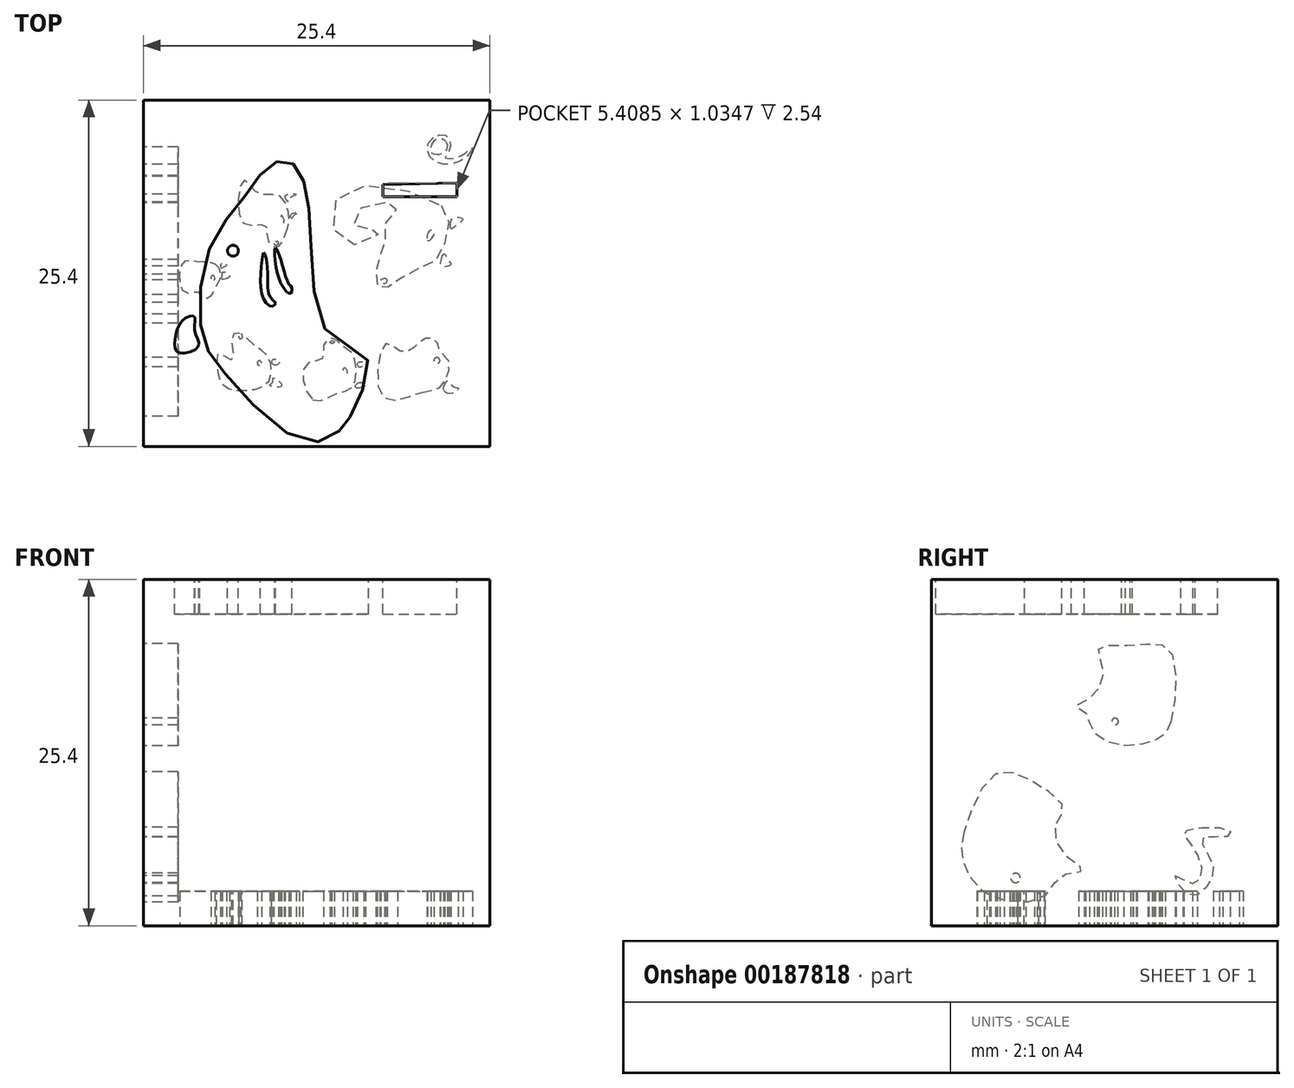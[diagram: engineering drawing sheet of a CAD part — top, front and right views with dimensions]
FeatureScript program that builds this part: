
annotation { "Feature Type Name" : "Feature", "Feature Type Description" : "" }
export const myFeature = defineFeature(function(context is Context, id is Id, definition is map)
    precondition{}
    {
        {
            var Q0;
            Q0=qCreatedBy(makeId("Front.planeOp"),FACE);
            var sketch = newSketch(context, id + "F0", { "sketchPlane" : qUnion([Q0])});
            skLineSegment(sketch, "E0.bottom", {"start": v(12.7, 12.7) * mm, "end": v(-12.7, 12.7) * mm});
            skLineSegment(sketch, "E0.top", {"start": v(12.7, -12.7) * mm, "end": v(-12.7, -12.7) * mm});
            skLineSegment(sketch, "E0.left", {"start": v(12.7, 12.7) * mm, "end": v(12.7, -12.7) * mm});
            skLineSegment(sketch, "E0.right", {"start": v(-12.7, 12.7) * mm, "end": v(-12.7, -12.7) * mm});
            skPoint(sketch, "E0.middle", {"position": v(0, 0) * mm});
            skSolve(sketch);
        }
        {
            var Q0;
            Q0 = qSketchRegion(id + "F0", true);
            extrude(context, id + "F1", {"entities" : qUnion([Q0]), "depth" : 25.4 * mm});
        }
        {
            var Q0;
            Q0=makeQuery(id+"F1.opExtrude","SWEPT_FACE",FACE,{"disambiguationData":[OSD([sQuery(id+"F0.wireOp",EDGE,"E0.bottom")])]});
            var sketch = newSketch(context, id + "F2", { "sketchPlane" : qUnion([Q0])});
            skFitSpline(sketch, "E1", {"points": [v(-6.7, -20.08) * mm, v(-8.4, -17.21) * mm, v(-7.88, -10.96) * mm, v(-5.3, -7.1) * mm, v(-3.55, -4.9) * mm, v(-2.1, -4.47) * mm, v(-1.06, -5.7) * mm, v(-0.45, -9.83) * mm, v(0.96, -17.26) * mm, v(3.7, -18.96) * mm, v(2.61, -22.9) * mm, v(1.72, -24.22) * mm, v(-0.87, -25.02) * mm, v(-6.7, -20.08) * mm]});
            skLineSegment(sketch, "E2", {"start": v(4.87, -7.1) * mm, "end": v(10.28, -7.1) * mm});
            skLineSegment(sketch, "E3", {"start": v(10.28, -7.1) * mm, "end": v(10.28, -6.07) * mm});
            skLineSegment(sketch, "E4", {"start": v(4.87, -7.1) * mm, "end": v(4.87, -6.2) * mm});
            skLineSegment(sketch, "E5", {"start": v(4.87, -6.2) * mm, "end": v(10.28, -6.07) * mm});
            skCircle(sketch, "E6", {"center": v(-6.14, -11.05) * mm, "radius": 0.4 * mm});
            skFitSpline(sketch, "E7", {"points": [v(-3.87, -11.18) * mm, v(-4.1, -12.55) * mm, v(-3.9, -14.57) * mm, v(-3.26, -15.14) * mm, v(-3.03, -14.87) * mm, v(-3.4, -14.45) * mm, v(-3.6, -12.62) * mm, v(-3.87, -11.18) * mm]});
            skFitSpline(sketch, "E8", {"points": [v(-3.03, -10.83) * mm, v(-3, -12.13) * mm, v(-2.42, -13.8) * mm, v(-1.92, -14.19) * mm, v(-1.8, -13.8) * mm, v(-2.08, -13.42) * mm, v(-2.53, -12.05) * mm, v(-3.03, -10.83) * mm]});
            skFitSpline(sketch, "E9", {"points": [v(-8.67, -18.06) * mm, v(-8.94, -16.94) * mm, v(-8.98, -15.9) * mm, v(-9.8, -16.13) * mm, v(-10.4, -17.55) * mm, v(-10.13, -18.54) * mm, v(-8.67, -18.06) * mm]});
            skSolve(sketch);
        }
        {
            var Q0;
            Q0=makeQuery(id+"F2.imprint","IMPRINT",FACE,{"disambiguationData":[TD([[makeQuery(id+"F2.imprint","IMPRINT",EDGE,{"derivedFrom":sQuery(id+"F2.wireOp",EDGE,"25fdf307-3059-4b63-b4c4-ef75757527ce")}),-1.0]])]});
            var Q1;
            Q1=makeQuery(id+"F2.imprint","IMPRINT",FACE,{"disambiguationData":[TD([[makeQuery(id+"F2.imprint","IMPRINT",EDGE,{"derivedFrom":sQuery(id+"F2.wireOp",EDGE,"E2")}),1.0]])]});
            var Q2;
            Q2=makeQuery(id+"F2.imprint","IMPRINT",FACE,{"disambiguationData":[TD([[makeQuery(id+"F2.imprint","IMPRINT",EDGE,{"derivedFrom":sQuery(id+"F2.wireOp",EDGE,"E1")}),-1.0]])]});
            var Q3;
            Q3=makeQuery(id+"F2.imprint","IMPRINT",FACE,{"disambiguationData":[TD([[makeQuery(id+"F2.imprint","IMPRINT",EDGE,{"derivedFrom":sQuery(id+"F2.wireOp",EDGE,"E9")}),1.0]])]});
            extrude(context, id + "F3", {"entities" : qUnion([Q0, Q1, Q2, Q3]), "operationType" : NewBodyOperationType.REMOVE, "oppositeDirection" : true, "depth" : 2.54 * mm});
        }
        {
            var Q0;
            Q0=makeQuery(id+"F1.opExtrude","SWEPT_FACE",FACE,{"disambiguationData":[OSD([sQuery(id+"F0.wireOp",EDGE,"E0.right")])]});
            var sketch = newSketch(context, id + "F4", { "sketchPlane" : qUnion([Q0])});
            skFitSpline(sketch, "E10", {"points": [v(23, -5.85) * mm, v(23.11, -7.79) * mm, v(21.38, -10.34) * mm, v(17.14, -10.56) * mm, v(15.85, -9.01) * mm, v(14.26, -8.65) * mm, v(15.7, -7.43) * mm, v(16.24, -5.13) * mm, v(15.7, -4.08) * mm, v(18.22, -2) * mm, v(20.84, -1.68) * mm, v(23, -5.85) * mm]});
            skFitSpline(sketch, "E11", {"points": [v(7.83, 2.28) * mm, v(8.62, 1.1) * mm, v(11.35, 0.52) * mm, v(13.62, 1.67) * mm, v(14.05, 2.9) * mm, v(14.84, 3.36) * mm, v(13.76, 4) * mm, v(12.79, 6.13) * mm, v(13.15, 7.6) * mm, v(10.52, 7.89) * mm, v(7.9, 7.5) * mm, v(7.83, 2.28) * mm]});
            skCircle(sketch, "E12", {"center": v(19.23, -9.2) * mm, "radius": 0.35 * mm});
            skCircle(sketch, "E13", {"center": v(11.93, 2.27) * mm, "radius": 0.24 * mm});
            skFitSpline(sketch, "E14", {"points": [v(7.52, -9.03) * mm, v(6.26, -9.6) * mm, v(5.55, -8.62) * mm, v(6.6, -6.38) * mm, v(6.8, -5.77) * mm, v(3.55, -5.7) * mm, v(3.65, -6.15) * mm, v(5.55, -6.28) * mm, v(4.87, -7.94) * mm, v(5, -9.54) * mm, v(6.47, -10.49) * mm, v(7.52, -9.03) * mm]});
            skSolve(sketch);
        }
        {
            var Q0;
            Q0 = qSketchRegion(id + "F4", true);
            extrude(context, id + "F5", {"entities" : qUnion([Q0]), "operationType" : NewBodyOperationType.REMOVE, "oppositeDirection" : true, "depth" : 2.54 * mm});
        }
        {
            var Q0;
            Q0=makeQuery(id+"F1.opExtrude","SWEPT_FACE",FACE,{"disambiguationData":[OSD([sQuery(id+"F0.wireOp",EDGE,"E0.top")])]});
            var sketch = newSketch(context, id + "F6", { "sketchPlane" : qUnion([Q0])});
            skFitSpline(sketch, "E15", {"points": [v(7.72, 21.44) * mm, v(9.16, 20.98) * mm, v(9.7, 19.2) * mm, v(9.06, 18.45) * mm, v(8.74, 17.62) * mm, v(7.88, 17.52) * mm, v(7.06, 18.22) * mm, v(6.08, 18.4) * mm, v(5.04, 17.87) * mm, v(4.82, 21.73) * mm, v(7.72, 21.44) * mm]});
            skFitSpline(sketch, "E16", {"points": [v(9.3, 21.23) * mm, v(9.65, 20.58) * mm, v(10, 21) * mm, v(10.39, 21.14) * mm, v(9.9, 21.52) * mm, v(9.3, 21.23) * mm]});
            skFitSpline(sketch, "E17", {"points": [v(9.13, 7.74) * mm, v(9.62, 9.43) * mm, v(8.76, 11.74) * mm, v(6.99, 12.55) * mm, v(5.47, 13.6) * mm, v(4.68, 13.8) * mm, v(4.38, 13.32) * mm, v(4.64, 11.4) * mm, v(5.06, 10.4) * mm, v(5.06, 9) * mm, v(5.92, 7.79) * mm, v(3.25, 7.94) * mm, v(2.9, 9.37) * mm, v(4.7, 9.56) * mm, v(2.22, 10.57) * mm, v(1.73, 6.91) * mm, v(9.13, 7.74) * mm]});
            skFitSpline(sketch, "E18", {"points": [v(9.85, 9.43) * mm, v(10, 8.66) * mm, v(10.7, 8.75) * mm, v(10.28, 9.13) * mm, v(9.85, 9.43) * mm]});
            skFitSpline(sketch, "E19", {"points": [v(9.13, 11.72) * mm, v(9.36, 11.3) * mm, v(9.62, 11.72) * mm, v(9.83, 12.08) * mm, v(9.21, 12.2) * mm, v(9.13, 11.72) * mm]});
            skCircle(sketch, "E20", {"center": v(8.81, 19.11) * mm, "radius": 0.22 * mm});
            skFitSpline(sketch, "E21", {"points": [v(8.12, 10.29) * mm, v(8.46, 10.12) * mm, v(8.57, 9.58) * mm, v(8.25, 9.63) * mm, v(8.12, 10.29) * mm]});
            skFitSpline(sketch, "E22", {"points": [v(-0.29, 21.97) * mm, v(1.4, 21.55) * mm, v(2.71, 20.91) * mm, v(2.63, 18.62) * mm, v(1.95, 18.11) * mm, v(1.26, 17.48) * mm, v(0.55, 17.9) * mm, v(0.4, 18.97) * mm, v(-0.84, 19.46) * mm, v(-0.29, 21.97) * mm]});
            skFitSpline(sketch, "E23", {"points": [v(2.89, 21.1) * mm, v(3.08, 20.73) * mm, v(3.57, 20.9) * mm, v(2.89, 21.1) * mm]});
            skFitSpline(sketch, "E24", {"points": [v(2.22, 20.06) * mm, v(2.1, 19.67) * mm, v(1.92, 19.8) * mm, v(2.22, 20.06) * mm]});
            skFitSpline(sketch, "E25", {"points": [v(-2.27, 9.82) * mm, v(-2.03, 8.85) * mm, v(-2.68, 7.05) * mm, v(-4.35, 6.81) * mm, v(-5.35, 5.91) * mm, v(-5.41, 9) * mm, v(-3.81, 9.17) * mm, v(-3.58, 10.3) * mm, v(-2.85, 10.76) * mm, v(-2.27, 9.82) * mm]});
            skFitSpline(sketch, "E26", {"points": [v(-2.07, 7.46) * mm, v(-2.3, 7.01) * mm, v(-1.49, 6.93) * mm, v(-2.01, 7.24) * mm, v(-2.07, 7.46) * mm]});
            skFitSpline(sketch, "E27", {"points": [v(-2.44, 8.97) * mm, v(-2.38, 8.8) * mm, v(-2.6, 8.47) * mm, v(-2.44, 8.97) * mm]});
            skFitSpline(sketch, "E28", {"points": [v(5.1, 13.41) * mm, v(5.07, 13.1) * mm, v(4.65, 13.31) * mm, v(5.1, 13.41) * mm]});
            skFitSpline(sketch, "E29", {"points": [v(11.42, 3.5) * mm, v(10.7, 4.4) * mm, v(8.55, 4.42) * mm, v(8.26, 3.03) * mm, v(9.52, 2.63) * mm, v(9.73, 3.73) * mm, v(9.39, 4.2) * mm, v(9.88, 4.29) * mm, v(10.95, 3.85) * mm, v(11.42, 3.5) * mm]});
            skFitSpline(sketch, "E30", {"points": [v(9.46, 3.03) * mm, v(9.39, 3.82) * mm, v(8.43, 3.87) * mm, v(8.74, 2.9) * mm, v(9.46, 3.03) * mm]});
            skFitSpline(sketch, "E31", {"points": [v(-7.28, 19.83) * mm, v(-7.06, 20.59) * mm, v(-6.52, 21.14) * mm, v(-5.37, 21.29) * mm, v(-3.93, 21.02) * mm, v(-3.32, 20.05) * mm, v(-3.66, 18.7) * mm, v(-4.54, 18.01) * mm, v(-5.64, 17.1) * mm, v(-6.22, 17.37) * mm, v(-6.2, 19.06) * mm, v(-7.17, 18.6) * mm, v(-7.28, 19.83) * mm]});
            skFitSpline(sketch, "E32", {"points": [v(-3.43, 20.93) * mm, v(-3.21, 20.68) * mm, v(-3.18, 20.37) * mm, v(-2.57, 20.96) * mm, v(-3.43, 20.93) * mm]});
            skFitSpline(sketch, "E33", {"points": [v(-5.64, 17.51) * mm, v(-5.64, 17.1) * mm, v(-5.46, 17.4) * mm, v(-5.64, 17.51) * mm]});
            skCircle(sketch, "E34", {"center": v(-4.2, 19.3) * mm, "radius": 0.16 * mm});
            skFitSpline(sketch, "E35", {"points": [v(-3.1, 19.45) * mm, v(-3.25, 19.06) * mm, v(-2.7, 19.17) * mm, v(-3.1, 19.45) * mm]});
            skFitSpline(sketch, "E36", {"points": [v(1.26, 17.65) * mm, v(1.2, 17.84) * mm, v(0.99, 17.75) * mm, v(1.26, 17.65) * mm]});
            skFitSpline(sketch, "E37", {"points": [v(-3.14, 10.52) * mm, v(-2.85, 10.6) * mm, v(-2.85, 10.39) * mm, v(-3.14, 10.52) * mm]});
            skFitSpline(sketch, "E38", {"points": [v(3.1, 19.6) * mm, v(3.06, 19.23) * mm, v(3.45, 19.32) * mm, v(3.1, 19.6) * mm]});
            skFitSpline(sketch, "E39", {"points": [v(-1.86, 8.7) * mm, v(-1.88, 8.39) * mm, v(-1.28, 8.25) * mm, v(-1.64, 8.44) * mm, v(-1.86, 8.7) * mm]});
            skFitSpline(sketch, "E40", {"points": [v(-7.46, 12.02) * mm, v(-7.05, 12.92) * mm, v(-7.53, 13.9) * mm, v(-7.83, 14.46) * mm, v(-8.4, 14.53) * mm, v(-8.66, 14.1) * mm, v(-9.7, 14.1) * mm, v(-9.8, 11.95) * mm, v(-8.83, 11.82) * mm, v(-7.46, 12.02) * mm]});
            skFitSpline(sketch, "E41", {"points": [v(-7.5, 13.2) * mm, v(-7.54, 12.89) * mm, v(-7.73, 12.94) * mm, v(-7.73, 13.14) * mm, v(-7.5, 13.2) * mm]});
            skFitSpline(sketch, "E42", {"points": [v(-6.97, 13.14) * mm, v(-6.92, 12.92) * mm, v(-6.88, 12.62) * mm, v(-6.37, 12.92) * mm, v(-6.97, 13.14) * mm]});
            skFitSpline(sketch, "E43", {"points": [v(-7.05, 12.07) * mm, v(-6.98, 12.3) * mm, v(-6.6, 12.05) * mm, v(-6.83, 11.97) * mm, v(-7.05, 12.07) * mm]});
            skSolve(sketch);
        }
        {
            var Q0;
            Q0=makeQuery(id+"F6.imprint","IMPRINT",FACE,{"disambiguationData":[TD([[makeQuery(id+"F6.imprint","IMPRINT",EDGE,{"derivedFrom":sQuery(id+"F6.wireOp",EDGE,"E15")}),-1.0]])]});
            var Q1;
            Q1=makeQuery(id+"F6.imprint","IMPRINT",FACE,{"disambiguationData":[TD([[makeQuery(id+"F6.imprint","IMPRINT",EDGE,{"derivedFrom":sQuery(id+"F6.wireOp",EDGE,"E16")}),1.0]])]});
            var Q2;
            Q2=makeQuery(id+"F6.imprint","IMPRINT",FACE,{"disambiguationData":[TD([[makeQuery(id+"F6.imprint","IMPRINT",EDGE,{"derivedFrom":sQuery(id+"F6.wireOp",EDGE,"E17")}),1.0]])]});
            var Q3;
            Q3=makeQuery(id+"F6.imprint","IMPRINT",FACE,{"disambiguationData":[TD([[makeQuery(id+"F6.imprint","IMPRINT",EDGE,{"derivedFrom":sQuery(id+"F6.wireOp",EDGE,"E19")}),1.0]])]});
            var Q4;
            Q4=makeQuery(id+"F6.imprint","IMPRINT",FACE,{"disambiguationData":[TD([[makeQuery(id+"F6.imprint","IMPRINT",EDGE,{"derivedFrom":sQuery(id+"F6.wireOp",EDGE,"E18")}),1.0]])]});
            var Q5;
            Q5=makeQuery(id+"F6.imprint","IMPRINT",FACE,{"disambiguationData":[TD([[makeQuery(id+"F6.imprint","IMPRINT",EDGE,{"derivedFrom":sQuery(id+"F6.wireOp",EDGE,"E29")}),1.0]])]});
            var Q6;
            Q6=makeQuery(id+"F6.imprint","IMPRINT",FACE,{"disambiguationData":[TD([[makeQuery(id+"F6.imprint","IMPRINT",EDGE,{"derivedFrom":sQuery(id+"F6.wireOp",EDGE,"E22")}),-1.0]])]});
            var Q7;
            Q7=makeQuery(id+"F6.imprint","IMPRINT",FACE,{"disambiguationData":[TD([[makeQuery(id+"F6.imprint","IMPRINT",EDGE,{"derivedFrom":sQuery(id+"F6.wireOp",EDGE,"E23")}),1.0]])]});
            var Q8;
            Q8=makeQuery(id+"F6.imprint","IMPRINT",FACE,{"disambiguationData":[TD([[makeQuery(id+"F6.imprint","IMPRINT",EDGE,{"derivedFrom":sQuery(id+"F6.wireOp",EDGE,"E38")}),1.0]])]});
            var Q9;
            Q9=makeQuery(id+"F6.imprint","IMPRINT",FACE,{"disambiguationData":[TD([[makeQuery(id+"F6.imprint","IMPRINT",EDGE,{"derivedFrom":sQuery(id+"F6.wireOp",EDGE,"E34")}),-1.0]])]});
            var Q10;
            Q10=makeQuery(id+"F6.imprint","IMPRINT",FACE,{"disambiguationData":[TD([[makeQuery(id+"F6.imprint","IMPRINT",EDGE,{"derivedFrom":sQuery(id+"F6.wireOp",EDGE,"E32")}),1.0]])]});
            var Q11;
            Q11=makeQuery(id+"F6.imprint","IMPRINT",FACE,{"disambiguationData":[TD([[makeQuery(id+"F6.imprint","IMPRINT",EDGE,{"derivedFrom":sQuery(id+"F6.wireOp",EDGE,"E35")}),1.0]])]});
            var Q12;
            Q12=makeQuery(id+"F6.imprint","IMPRINT",FACE,{"disambiguationData":[TD([[makeQuery(id+"F6.imprint","IMPRINT",EDGE,{"derivedFrom":sQuery(id+"F6.wireOp",EDGE,"E40")}),1.0]])]});
            var Q13;
            Q13=makeQuery(id+"F6.imprint","IMPRINT",FACE,{"disambiguationData":[TD([[makeQuery(id+"F6.imprint","IMPRINT",EDGE,{"derivedFrom":sQuery(id+"F6.wireOp",EDGE,"E42")}),1.0]])]});
            var Q14;
            Q14=makeQuery(id+"F6.imprint","IMPRINT",FACE,{"disambiguationData":[TD([[makeQuery(id+"F6.imprint","IMPRINT",EDGE,{"derivedFrom":sQuery(id+"F6.wireOp",EDGE,"E43")}),-1.0]])]});
            var Q15;
            Q15=makeQuery(id+"F6.imprint","IMPRINT",FACE,{"disambiguationData":[TD([[makeQuery(id+"F6.imprint","IMPRINT",EDGE,{"derivedFrom":sQuery(id+"F6.wireOp",EDGE,"E25")}),-1.0]])]});
            var Q16;
            Q16=makeQuery(id+"F6.imprint","IMPRINT",FACE,{"disambiguationData":[TD([[makeQuery(id+"F6.imprint","IMPRINT",EDGE,{"derivedFrom":sQuery(id+"F6.wireOp",EDGE,"E39")}),1.0]])]});
            var Q17;
            Q17=makeQuery(id+"F6.imprint","IMPRINT",FACE,{"disambiguationData":[TD([[makeQuery(id+"F6.imprint","IMPRINT",EDGE,{"derivedFrom":sQuery(id+"F6.wireOp",EDGE,"E26")}),1.0]])]});
            extrude(context, id + "F7", {"entities" : qUnion([Q0, Q1, Q2, Q3, Q4, Q5, Q6, Q7, Q8, Q9, Q10, Q11, Q12, Q13, Q14, Q15, Q16, Q17]), "operationType" : NewBodyOperationType.REMOVE, "oppositeDirection" : true, "depth" : 2.54 * mm});
        }
    });
